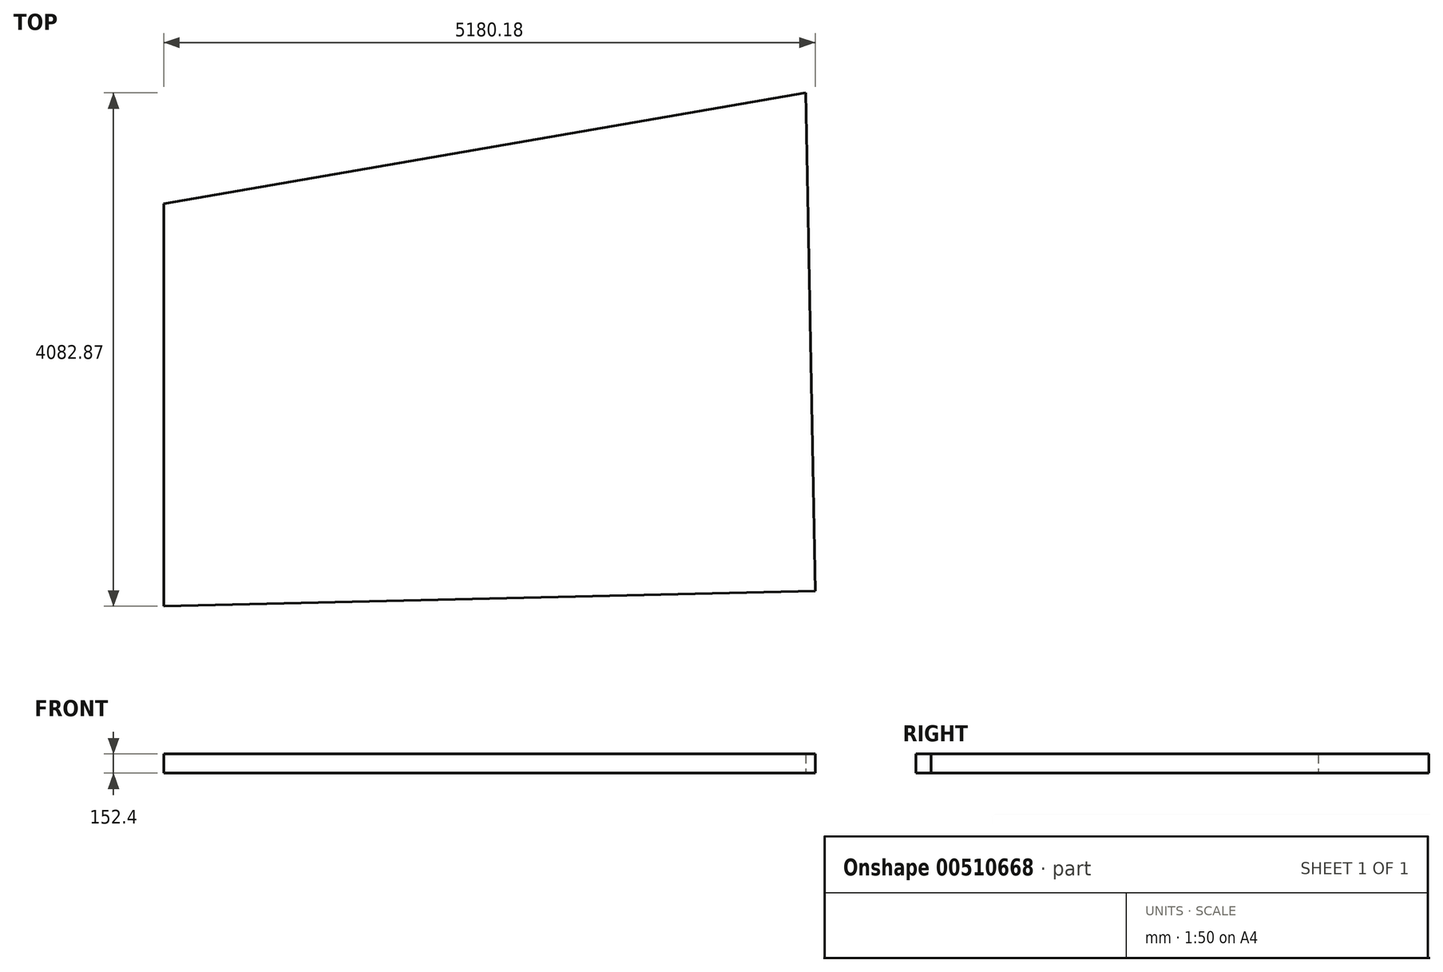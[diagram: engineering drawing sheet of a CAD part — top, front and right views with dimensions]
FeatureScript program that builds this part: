
annotation { "Feature Type Name" : "Feature", "Feature Type Description" : "" }
export const myFeature = defineFeature(function(context is Context, id is Id, definition is map)
    precondition{}
    {
        {
            var Q0;
            Q0=qCreatedBy(makeId("Top.planeOp"),FACE);
            var sketch = newSketch(context, id + "F0", { "sketchPlane" : qUnion([Q0])});
            skLineSegment(sketch, "E0", {"start": v(-5180.18, -144.32) * mm, "end": v(-5180.18, 3056.08) * mm});
            skLineSegment(sketch, "E1", {"start": v(-5180.18, 3056.08) * mm, "end": v(-74.28, 3938.55) * mm});
            skLineSegment(sketch, "E2", {"start": v(-74.28, 3938.55) * mm, "end": v(0, -23.15) * mm});
            skLineSegment(sketch, "E3", {"start": v(0, -23.15) * mm, "end": v(-5180.18, -144.32) * mm});
            skSolve(sketch);
        }
        {
            var Q0;
            Q0 = qSketchRegion(id + "F0", true);
            extrude(context, id + "F1", {"entities" : qUnion([Q0]), "depth" : 152.4 * mm, "offsetDistance" : 30.48 * mm});
        }
    });
